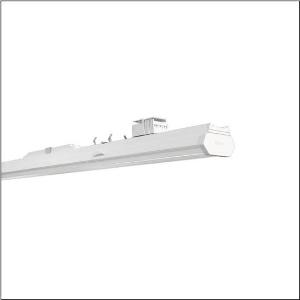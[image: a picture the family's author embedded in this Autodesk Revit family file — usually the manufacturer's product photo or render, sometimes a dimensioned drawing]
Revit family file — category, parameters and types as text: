
# Revit family: licross_r__21_protected_ho_52td12cn4cxm_6843
name_source: partatom
category: Lighting Fixtures
units: mm (PartAtom-declared; Revit-internal decimal feet)

## family parameters
Cut with Voids When Loaded = No
Host = Face
Light Source = No
Part Type = Normal
Room Calculation Point = No
Round Connector Dimension = Use Diameter
Shared = No

## types (1)
- --- (1 x LED, 12460 lm, 68.9 W, 4000K)
    Apparent Load = 69 VA
    CIE Flux Codes = 70 91 97 98 100
    Color Rendering = 80
    Color Temperature = 4000K
    Default Elevation = 1800 mm
    Description = Licross® 21 Protected HO, luminaire insert, of sheet steel, galvanised, coil coated, white, length: 1.500mm, width: 90mm, height: 103mm, LED rated luminous flux: 12.460lm, light colour: 840, control gear: ON/OFF Multilumen, CLOi, control gear: ECG Multilumen, with plug, 3-pole, with phase selection, mains connection: 220..240V, AC, 50/60Hz, start of lifetime: 69W, end of service life: 83W, halogen-free wiring, primary light control with lens, of plastic, primary optical cover: cover, of PMMA, light emission: direct distribution, primary light characteristic: symmetric, protection rating (complete): IP54, insulation class (complete): insulation class I (protective earthing), certification: CE, ENEC, VDE, UKCA, protection symbol: D if used in an environment with non-conductive dust loads with corresponding accessories, impact resistance: IK06, permissible ambient temperature for indoor applications: -35..+35°C, corresponds to IFS (International Featured Standards) requirements for safety and quality in the food industry, reducing of maximum allowable ambient temperature of 5°C with ceiling mounting, LABS conformity tested according to VDMA 24364:2018-05, packaging unit: 1 piece
    Height = 92 mm
    Lamp = 1 x LED
    Lamp Light Flux = 12460 lm
    Lamp Power = 68.9 W
    Lamp count = 1
    Length = 1500 mm
    Luminous efficacy = 181 lm/W
    Manufacturer = Siteco
    ModVariant = No
    Model = 52TD12CN4CXM
    Mounting Place = Ceiling
    Mounting Type = Pendant
    Number of Poles = 1
    OnlyDefault = Yes
    Power Factor = 1
    Product Name = Licross® 21 Protected HO
    Product group = luminaire insert
    ProductGroupID = 901
    Protection Class = Protection class I
    Protection Degree = IP 54
    RLX_Detail_Level = 1
    RLX_Emergency_Light_Flux = 0 lm
    RLX_Emergency_Type = 0
    RLX_Emergency_Type_DB = No
    RlxData = <blob elided: 22125 chars, md5=50db641c>
    Socket = socket
    Standby Power = 0 W
    System Light Flux = 12460 lm
    System Power = 69 W
    Type Comments = factory setting: luminous flux: 100 % | (A | C | E) | 162 mA
    Type Image = l_1256148.jpg
    URL = http://relux.com
    VarID = @adj_041585
    Voltage = 0 V
    Weight = 0.00 kg
    Width = 88 mm

## geometry (parser evidence)
native form markers: Blend x4, Sweep x10
no freeform markers — native parametric forms only
